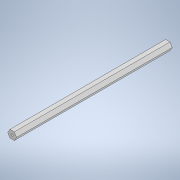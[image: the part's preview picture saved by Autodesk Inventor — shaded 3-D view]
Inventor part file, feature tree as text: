
AUTODESK INVENTOR PART (.ipt)
format: ipt  version: 2022.2 (Build 262287010, 287A)  size: 103,424 bytes
history: native  units: in
note: dims shown in document units (in); Inventor stores cm internally (conversion verified against a paired STEP export)
features: extrude x1, sketch x1
ambient origin geometry x8: Origin, YZ Plane, XZ Plane, XY Plane, X Axis, Y Axis, Z Axis, Center Point
bodies: Body1 (feature_tree)
feature tree (2):
  extrude  "Extrusion2"  Depth=7.75in
  sketch  "Sketch1"  dims[d0=0.375in d3=0.1in d4=7.75in d5=0.0in]
